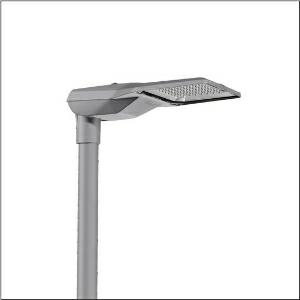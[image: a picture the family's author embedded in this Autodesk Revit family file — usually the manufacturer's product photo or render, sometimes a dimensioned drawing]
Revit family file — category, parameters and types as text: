
# Revit family: streetlight_sl_21_midi___stw1_0a_5xe3e43s08lb_9506
name_source: partatom
category: Lighting Fixtures
units: mm (PartAtom-declared; Revit-internal decimal feet)

## family parameters
Cut with Voids When Loaded = No
Host = Face
Light Source = No
Part Type = Normal
Room Calculation Point = No
Round Connector Dimension = Use Diameter
Shared = No

## types (1)
- --- (1 x LED, 14950 lm, 99.6 W, 4000K)
    Apparent Load = 100 VA
    CIE Flux Codes = 38 75 98 100 100
    Color Rendering = 70
    Color Temperature = 4000K
    Default Elevation = 1800 mm
    Description = Streetlight SL 21 midi, mast luminaire, primary light control with lens, of PMMA, primary optical cover: cover, of toughened safety glass, transparent, light distribution: STW1.0a, light emission: direct distribution, primary light characteristic: asymmetric, installation type: side-entry, post-top, LED, High Power LED, rated luminous flux: 14.950lm, luminous efficacy: 150lm/W, light colour: 740, colour temperature: 4000K, control gear: D4i, control: overheat protection, constant luminous flux control, time-dependent luminous flux control, flexible luminous flux parameterisation, pre-setting: logarithmic dimming characteristic, mains connection: 230..240V, AC, 50/60Hz, start of lifetime: 100W, end of service life: 102W, reduction: 46W, luminaire housing, of diecast aluminium, powder-coated, Siteco® metallic grey (DB 702S), corrosivity category C5 mid according to DIN EN ISO 12944, please order mast flange separately, inclination adjustable: 0°, 5°, 10°, 15°, sealing non-destructively replaceable, multi-level sealing system, length: 644mm, width: 335mm, height: 110mm, mast flange for spigot size: 42mm (side-entry): 5XC10008XM4, 60/48mm (side-entry/post-top): 5XC10108XM2, 76/60mm (side-entry/post-top): 5XC10108XM1, mounting height: 4..8m, Smart Interface above, protection rating (complete): IP66, insulation class (complete): insulation class II (safety insulation), certification: CE, ENEC, ENEC+, VDE, impact resistance: IK10, permissible operating ambient temperature for outdoor applications: -40..+50°C, standard-compliant lighting for roads and squares, packaging unit: 1 piece

Light Distribution: STW1.0a
    Height = 111 mm
    Lamp = 1 x LED
    Lamp Light Flux = 14950 lm
    Lamp Power = 99.6 W
    Lamp count = 1
    Length = 644 mm
    Luminous efficacy = 150 lm/W
    Manufacturer = Siteco
    ModVariant = No
    Model = 5XE3E43S08LB
    Number of Poles = 1
    OnlyDefault = Yes
    Power Factor = 1
    Product Name = Streetlight SL 21 midi | STW1.0a
    Product group = mast luminaire | pylon top
    ProductGroupID = 6100
    Protection Class = Protection class II
    Protection Degree = IP 66
    RLX_Detail_Level = 1
    RLX_Emergency_Light_Flux = 0 lm
    RLX_Emergency_Type = 0
    RLX_Emergency_Type_DB = No
    RlxData = <blob elided: 26809 chars, md5=e68544aa>
    Socket = socket
    Standby Power = 0 W
    System Light Flux = 14950 lm
    System Power = 100 W
    Type Comments = factory setting: luminous flux: 100 % | dim-lin: 254 | 1020 mA
    Type Image = l_1004302.jpg
    URL = http://relux.com
    VarID = @adj_031857
    Voltage = 0 V
    Weight = 0.00 kg
    Width = 336 mm

## geometry (parser evidence)
native form markers: Blend x4, Sweep x11
no freeform markers — native parametric forms only
